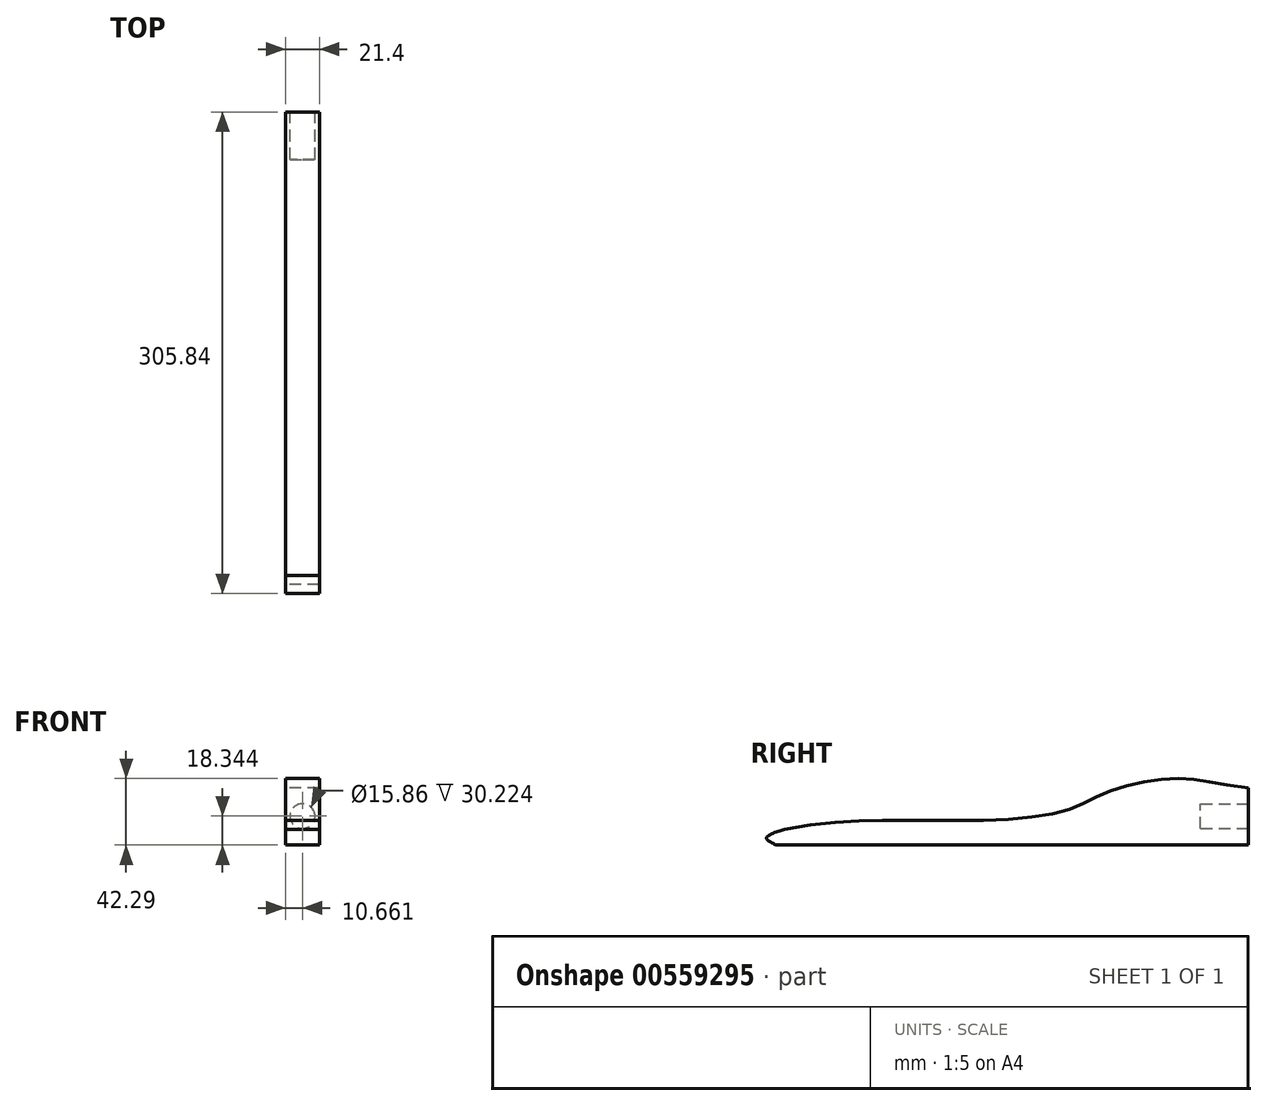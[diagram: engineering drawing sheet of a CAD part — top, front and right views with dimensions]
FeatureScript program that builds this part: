
annotation { "Feature Type Name" : "Feature", "Feature Type Description" : "" }
export const myFeature = defineFeature(function(context is Context, id is Id, definition is map)
    precondition{}
    {
        {
            var Q0;
            Q0=qCreatedBy(makeId("Right.planeOp"),FACE);
            var sketch = newSketch(context, id + "F0", { "sketchPlane" : qUnion([Q0])});
            skFitSpline(sketch, "E0", {"points": [v(-52.96, 20.32) * mm, v(-64.3, 14.97) * mm, v(-58.45, 10.43) * mm], "startDerivative": vector(-18.32, -4.53) * mm, "endDerivative": vector(17.71, -11.33) * mm});
            skLineSegment(sketch, "E1", {"start": v(-58.45, 10.43) * mm, "end": v(241.52, 10.43) * mm});
            skLineSegment(sketch, "E2", {"start": v(241.52, 10.43) * mm, "end": v(241.52, 46.75) * mm});
            skFitSpline(sketch, "E3", {"points": [v(-52.96, 20.32) * mm, v(35.45, 25.98) * mm, v(120.7, 31.01) * mm, v(152.8, 44.23) * mm, v(196.22, 52.72) * mm, v(241.52, 46.75) * mm], "startDerivative": vector(397.27, 77.68) * mm, "endDerivative": vector(343.53, -34) * mm});
            skSolve(sketch);
        }
        {
            var Q0;
            Q0=makeQuery(id+"F0.imprint","IMPRINT",FACE,{"disambiguationData":[TD([[makeQuery(id+"F0.imprint","IMPRINT",EDGE,{"derivedFrom":sQuery(id+"F0.wireOp",EDGE,"E0")}),1.0]])]});
            extrude(context, id + "F1", {"entities" : qUnion([Q0]), "depth" : 21.4 * mm, "offsetDistance" : 25 * mm});
        }
        {
            var Q0;
            Q0=qCreatedBy(makeId("Front.planeOp"),FACE);
            cPlane(context, id + "F2", {"entities" : qUnion([Q0]), "cplaneType" : CPlaneType.OFFSET, "offset" : 246 * mm, "oppositeDirection" : true, "width" : 150 * mm, "height" : 150 * mm});
        }
        {
            var Q0;
            Q0=qCreatedBy(id+"F2.planeOp",FACE);
            var sketch = newSketch(context, id + "F3", { "sketchPlane" : qUnion([Q0])});
            skCircle(sketch, "E4", {"center": v(10.66, 28.77) * mm, "radius": 7.93 * mm});
            skSolve(sketch);
        }
        {
            var Q0;
            Q0 = qSketchRegion(id + "F3", true);
            extrude(context, id + "F4", {"entities" : qUnion([Q0]), "operationType" : NewBodyOperationType.REMOVE, "depth" : 34.7 * mm, "offsetDistance" : 25 * mm});
        }
    });
